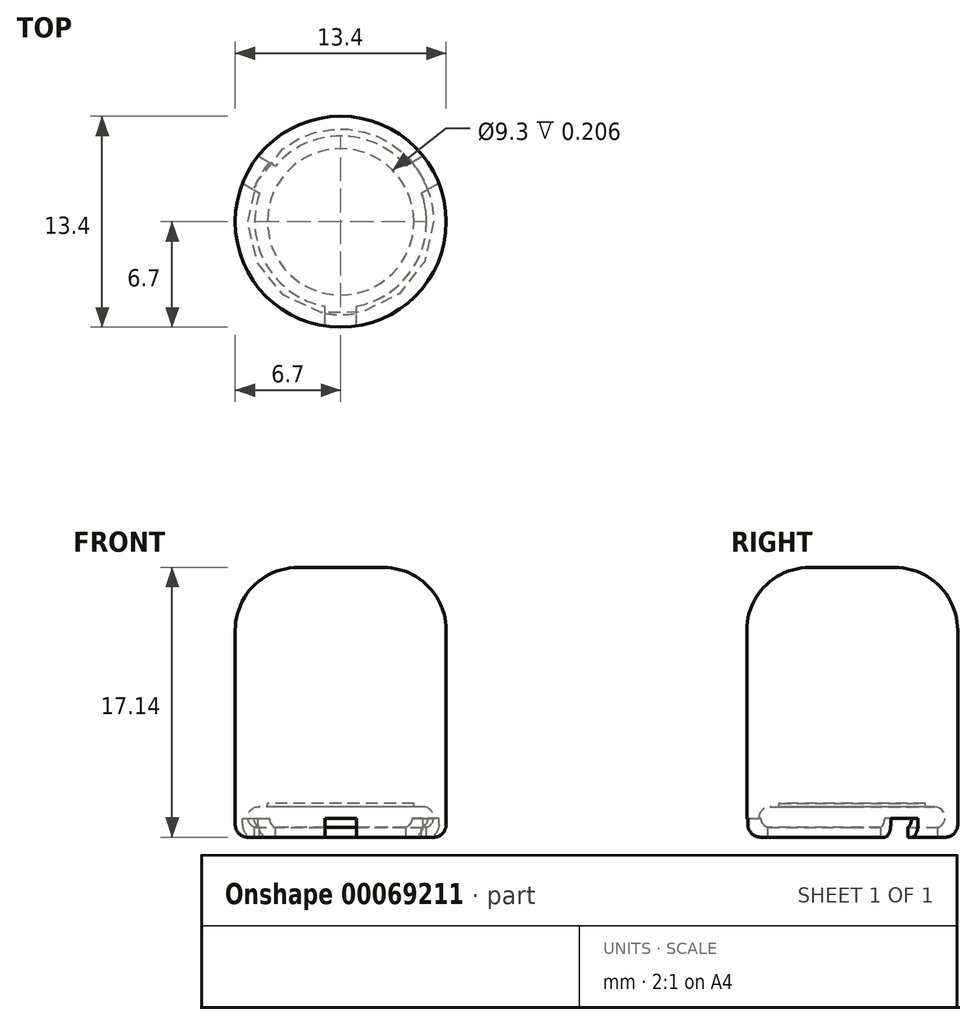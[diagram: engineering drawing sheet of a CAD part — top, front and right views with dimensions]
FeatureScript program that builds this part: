
annotation { "Feature Type Name" : "Feature", "Feature Type Description" : "" }
export const myFeature = defineFeature(function(context is Context, id is Id, definition is map)
    precondition{}
    {
        {
            var Q0;
            Q0=qCreatedBy(makeId("Front.planeOp"),FACE);
            var sketch = newSketch(context, id + "F0", { "sketchPlane" : qUnion([Q0])});
            skLineSegment(sketch, "E0", {"start": v(0, 1.35) * mm, "end": v(0, 0) * mm, "construction": true});
            skLineSegment(sketch, "E1.top", {"start": v(0, 1.56) * mm, "end": v(-4.65, 1.56) * mm});
            skLineSegment(sketch, "E1.left", {"start": v(0, 1.35) * mm, "end": v(0, 1.56) * mm});
            skLineSegment(sketch, "E1.right", {"start": v(-4.65, 1.35) * mm, "end": v(-4.65, 1.56) * mm});
            skLineSegment(sketch, "E2", {"start": v(-6.7, -0.58) * mm, "end": v(-6.7, 12.56) * mm});
            skLineSegment(sketch, "E3", {"start": v(-2.7, 16.56) * mm, "end": v(0, 16.56) * mm});
            skLineSegment(sketch, "E4", {"start": v(0, 16.56) * mm, "end": v(0, 1.56) * mm});
            skPoint(sketch, "E5.visualSharp", {"position": v(-6.7, 16.56) * mm});
            skArc(sketch, "E5.filletArc", {"start": v(-2.7, 16.56) * mm, "mid": v(-5.53, 15.38) * mm, "end": v(-6.7, 12.56) * mm});
            skLineSegment(sketch, "E6.bottom", {"start": v(0, 0) * mm, "end": v(-5.9, 0) * mm, "construction": true});
            skLineSegment(sketch, "E6.top", {"start": v(0, 1.35) * mm, "end": v(-5.9, 1.35) * mm, "construction": true});
            skLineSegment(sketch, "E6.left", {"start": v(0, 0) * mm, "end": v(0, 1.35) * mm, "construction": true});
            skLineSegment(sketch, "E6.right", {"start": v(-5.9, 0) * mm, "end": v(-5.9, 0.67) * mm, "construction": true});
            skLineSegment(sketch, "E7", {"start": v(-5.9, 0.67) * mm, "end": v(-5.23, 0.67) * mm, "construction": true});
            skLineSegment(sketch, "E8", {"start": v(-5.9, 0.67) * mm, "end": v(-5.9, 1.35) * mm, "construction": true});
            skArc(sketch, "E9", {"start": v(-5.9, 0.67) * mm, "mid": v(-5.7, 1.15) * mm, "end": v(-5.23, 1.35) * mm});
            skLineSegment(sketch, "E10", {"start": v(-5.23, 1.35) * mm, "end": v(-4.65, 1.35) * mm});
            skArc(sketch, "E11", {"start": v(-5.9, 0.67) * mm, "mid": v(-5.78, 0.29) * mm, "end": v(-5.46, 0.04) * mm});
            skLineSegment(sketch, "E12", {"start": v(-5.23, 0.67) * mm, "end": v(-5.46, 0.04) * mm, "construction": true});
            skLineSegment(sketch, "E13", {"start": v(-5.46, 0.04) * mm, "end": v(-5.46, -0.58) * mm});
            skLineSegment(sketch, "E14", {"start": v(-5.46, -0.58) * mm, "end": v(-6.7, -0.58) * mm});
            skLineSegment(sketch, "E15", {"start": v(-5.9, 0.67) * mm, "end": v(-6.7, 0.67) * mm, "construction": true});
            skSolve(sketch);
        }
        {
            var Q0;
            Q0=qSketchRegion(id+"F0",true);
            var Q1;
            Q1=sQuery(id+"F0.wireOp",EDGE,"E4");
            revolve(context, id + "F1", {"entities" : qUnion([Q0]), "axis" : qUnion([Q1]), "revolveType" : RevolveType.FULL});
        }
        {
            var Q0;
            Q0=makeQuery(id+"F1.opRevolve","SWEPT_FACE",FACE,{"disambiguationData":[OSD([sQuery(id+"F0.wireOp",EDGE,"E14")])]});
            var sketch = newSketch(context, id + "F2", { "sketchPlane" : qUnion([Q0])});
            skLineSegment(sketch, "E16.bottom", {"start": v(-1, 10) * mm, "end": v(1, 10) * mm});
            skLineSegment(sketch, "E16.top", {"start": v(-1, 0) * mm, "end": v(1, 0) * mm});
            skLineSegment(sketch, "E16.left", {"start": v(-1, 10) * mm, "end": v(-1, 0) * mm});
            skLineSegment(sketch, "E16.right", {"start": v(1, 10) * mm, "end": v(1, 0) * mm});
            skLineSegment(sketch, "E17.1.0", {"start": v(-8.16, -5.87) * mm, "end": v(-9.16, -4.13) * mm});
            skLineSegment(sketch, "E17.1.1", {"start": v(-8.16, -5.87) * mm, "end": v(0.5, -0.87) * mm});
            skLineSegment(sketch, "E17.1.2", {"start": v(-9.16, -4.13) * mm, "end": v(-0.5, 0.87) * mm});
            skLineSegment(sketch, "E17.1.3", {"start": v(0.5, -0.87) * mm, "end": v(-0.5, 0.87) * mm});
            skLineSegment(sketch, "E17.2.0", {"start": v(9.16, -4.13) * mm, "end": v(8.16, -5.87) * mm});
            skLineSegment(sketch, "E17.2.1", {"start": v(9.16, -4.13) * mm, "end": v(0.5, 0.87) * mm});
            skLineSegment(sketch, "E17.2.2", {"start": v(8.16, -5.87) * mm, "end": v(-0.5, -0.87) * mm});
            skLineSegment(sketch, "E17.2.3", {"start": v(0.5, 0.87) * mm, "end": v(-0.5, -0.87) * mm});
            skPoint(sketch, "E17.center", {"position": v(0, 0) * mm});
            skSolve(sketch);
        }
        {
            var Q0;
            Q0=makeQuery(id+"F1.opRevolve","SWEPT_EDGE",EDGE,{"disambiguationData":[OSD([sQuery(id+"F0.wireOp",EDGE,"E2"),sQuery(id+"F0.wireOp",EDGE,"E14")])]});
            fillet(context, id + "F3", {"entities" : qUnion([Q0]), "radius" : 0.8 * mm, "allowEdgeOverflow" : false});
        }
        {
            var Q0;
            Q0=qSketchRegion(id+"F2",true);
            extrude(context, id + "F4", {"entities" : qUnion([Q0]), "operationType" : NewBodyOperationType.REMOVE, "oppositeDirection" : true, "depth" : 1.2 * mm});
        }
    });
